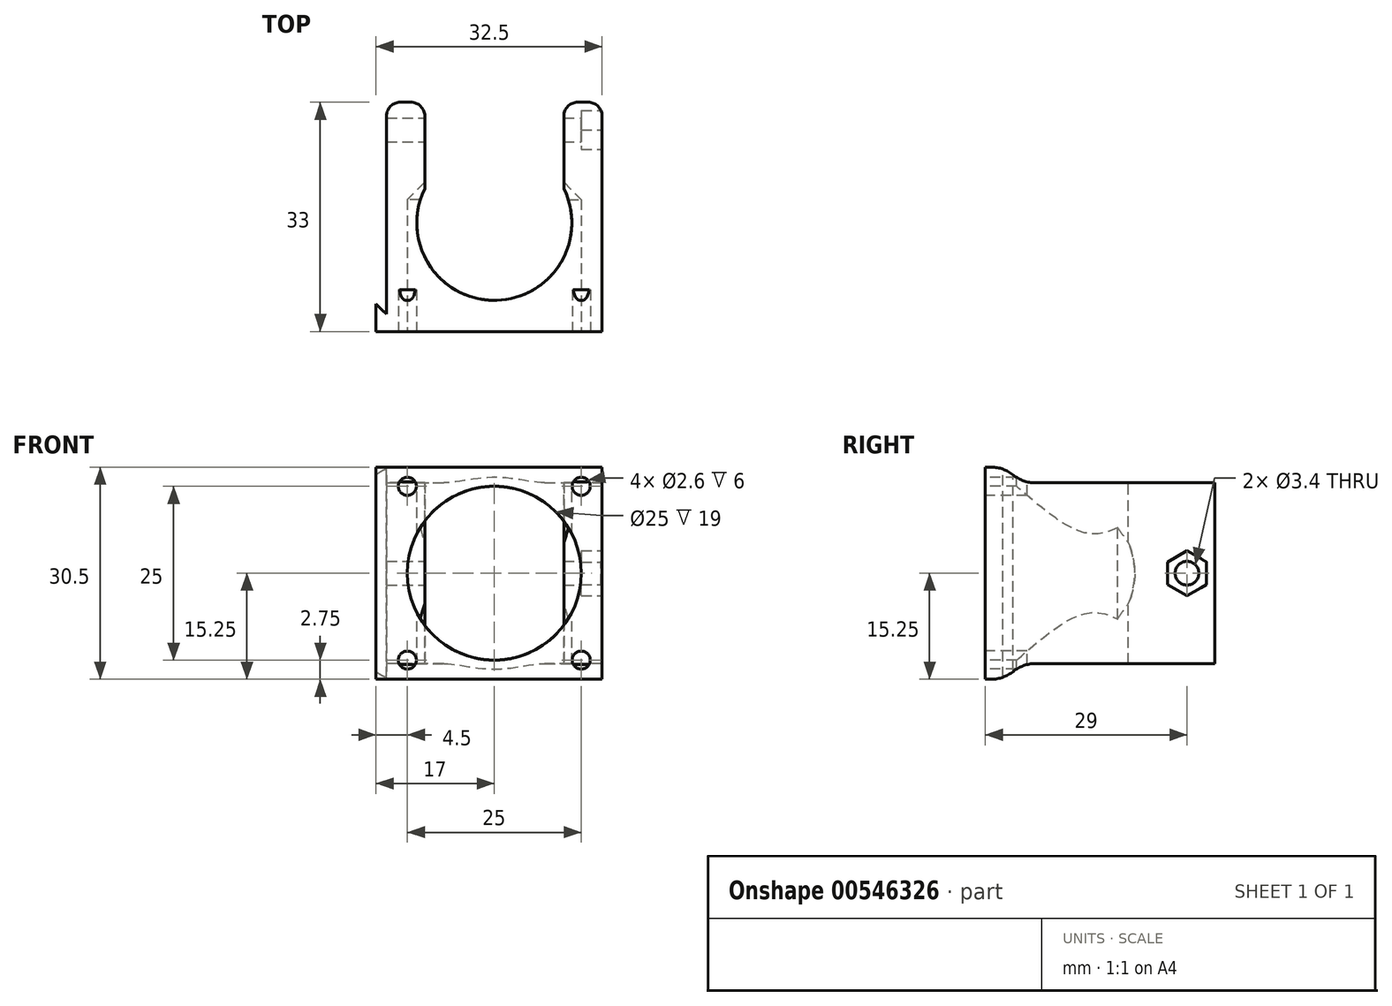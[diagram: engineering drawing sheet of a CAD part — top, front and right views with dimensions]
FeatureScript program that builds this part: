
annotation { "Feature Type Name" : "Feature", "Feature Type Description" : "" }
export const myFeature = defineFeature(function(context is Context, id is Id, definition is map)
    precondition{}
    {
        {
            var Q0;
            Q0=qCreatedBy(makeId("Top.planeOp"),FACE);
            var sketch = newSketch(context, id + "F0", { "sketchPlane" : qUnion([Q0])});
            skLineSegment(sketch, "E0.bottom", {"start": v(15.5, 16.5) * mm, "end": v(-15.5, 16.5) * mm});
            skLineSegment(sketch, "E0.top", {"start": v(15.5, -16.5) * mm, "end": v(-15.5, -16.5) * mm});
            skLineSegment(sketch, "E0.left", {"start": v(15.5, 16.5) * mm, "end": v(15.5, -16.5) * mm});
            skLineSegment(sketch, "E0.right", {"start": v(-15.5, 16.5) * mm, "end": v(-15.5, -16.5) * mm});
            skPoint(sketch, "E0.middle", {"position": v(0, 0) * mm});
            skLineSegment(sketch, "E1.bottom", {"start": v(-10, 16.5) * mm, "end": v(10, 16.5) * mm});
            skLineSegment(sketch, "E1.top", {"start": v(-10, 3.5) * mm, "end": v(10, 3.5) * mm});
            skLineSegment(sketch, "E1.left", {"start": v(-10, 16.5) * mm, "end": v(-10, 3.5) * mm});
            skLineSegment(sketch, "E1.right", {"start": v(10, 16.5) * mm, "end": v(10, 3.5) * mm});
            skSolve(sketch);
        }
        {
            var Q0;
            {var subQ0=sQuery(id+"F0.wireOp",EDGE,"E0.top");Q0=makeQuery(id+"F0.imprint","IMPRINT",FACE,{"disambiguationData":[TD([[makeQuery(id+"F0.imprint","IMPRINT",EDGE,{"derivedFrom":subQ0}),-1.0]])]});}
            extrude(context, id + "F1", {"entities" : qUnion([Q0]), "depth" : 30.5 * mm, "offsetDistance" : 25 * mm});
        }
        {
            var Q0;
            Q0=makeQuery(id+"F1.opExtrude","SWEPT_FACE",FACE,{"disambiguationData":[OSD([sQuery(id+"F0.wireOp",EDGE,"E0.top")])]});
            var sketch = newSketch(context, id + "F2", { "sketchPlane" : qUnion([Q0])});
            skCircle(sketch, "E2", {"center": v(0, 15.25) * mm, "radius": 12.5 * mm});
            skLineSegment(sketch, "E3", {"start": v(0, 15.25) * mm, "end": v(0, 30.5) * mm, "construction": true});
            skSolve(sketch);
        }
        {
            var Q0;
            Q0=makeQuery(id+"F2.imprint","IMPRINT",FACE,{"disambiguationData":[TD([[makeQuery(id+"F2.imprint","IMPRINT",EDGE,{"derivedFrom":sQuery(id+"F2.wireOp",EDGE,"E2")}),1.0]])]});
            extrude(context, id + "F3", {"entities" : qUnion([Q0]), "operationType" : NewBodyOperationType.REMOVE, "oppositeDirection" : true, "depth" : 22 * mm, "offsetDistance" : 25 * mm});
        }
        {
            var Q0;
            Q0=makeQuery(id+"F1.opExtrude","SWEPT_FACE",FACE,{"disambiguationData":[OSD([sQuery(id+"F0.wireOp",EDGE,"E0.right")])]});
            var sketch = newSketch(context, id + "F4", { "sketchPlane" : qUnion([Q0])});
            skSolve(sketch);
        }
        {
            var Q0;
            {var subQ0=sQuery(id+"F0.wireOp",EDGE,"E0.right");Q0=makeQuery(id+"F4.imprint","IMPRINT",FACE,{"disambiguationData":[TD([[makeQuery(id+"F4.imprint","IMPRINT",EDGE,{"derivedFrom":makeQuery(id+"F1.opExtrude","CAP_EDGE",EDGE,{"disambiguationData":[OSD([subQ0])],"isStart":true})}),1.0]])]});}
            var sketch = newSketch(context, id + "F5", { "sketchPlane" : qUnion([Q0])});
            skLineSegment(sketch, "E4.bottom", {"start": v(13.5, 0) * mm, "end": v(-21.5, 0) * mm});
            skLineSegment(sketch, "E4.top", {"start": v(13.5, 2.25) * mm, "end": v(-21.5, 2.25) * mm});
            skLineSegment(sketch, "E4.left", {"start": v(13.5, 0) * mm, "end": v(13.5, 2.25) * mm});
            skLineSegment(sketch, "E4.right", {"start": v(-21.5, 0) * mm, "end": v(-21.5, 2.25) * mm});
            skLineSegment(sketch, "E5.bottom", {"start": v(13.5, 28.25) * mm, "end": v(-21.5, 28.25) * mm});
            skLineSegment(sketch, "E5.top", {"start": v(13.5, 30.5) * mm, "end": v(-21.5, 30.5) * mm});
            skLineSegment(sketch, "E5.left", {"start": v(13.5, 28.25) * mm, "end": v(13.5, 30.5) * mm});
            skLineSegment(sketch, "E5.right", {"start": v(-21.5, 28.25) * mm, "end": v(-21.5, 30.5) * mm});
            skSolve(sketch);
        }
        {
            var Q0;
            {var subQ4=sQuery(id+"F5.wireOp",EDGE,"E4.right");Q0=makeQuery(id+"F5.imprint","IMPRINT",FACE,{"disambiguationData":[TD([[makeQuery(id+"F5.imprint","IMPRINT",EDGE,{"derivedFrom":subQ4}),-1.0]])]});}
            var Q1;
            {var subQ4=sQuery(id+"F5.wireOp",EDGE,"E4.left");Q1=makeQuery(id+"F5.imprint","IMPRINT",FACE,{"disambiguationData":[TD([[makeQuery(id+"F5.imprint","IMPRINT",EDGE,{"derivedFrom":subQ4}),1.0]])]});}
            var Q2;
            {var subQ0=sQuery(id+"F5.wireOp",EDGE,"E5.left");Q2=makeQuery(id+"F5.imprint","IMPRINT",FACE,{"disambiguationData":[TD([[makeQuery(id+"F5.imprint","IMPRINT",EDGE,{"derivedFrom":subQ0}),1.0]])]});}
            extrude(context, id + "F6", {"entities" : qUnion([Q0, Q1, Q2]), "operationType" : NewBodyOperationType.REMOVE, "oppositeDirection" : true, "depth" : 50 * mm, "offsetDistance" : 25 * mm});
        }
        {
            var Q0;
            {var subQ0=sQuery(id+"F5.wireOp",EDGE,"E4.top");var subQ1=sQuery(id+"F5.wireOp",EDGE,"E4.left");Q0=makeQuery(id+"F6.boolean.opBoolean","COPY",EDGE,{"disambiguationData":[TD([makeQuery(id+"F1.opExtrude","SWEPT_FACE",FACE,{"disambiguationData":[OSD([sQuery(id+"F0.wireOp",EDGE,"E0.right")])]})])],"derivedFrom":makeQuery(id+"F6.opExtrude","SWEPT_EDGE",EDGE,{"disambiguationData":[OSD([subQ0,subQ1])]})});}
            var Q1;
            {var subQ0=sQuery(id+"F5.wireOp",EDGE,"E4.top");var subQ1=sQuery(id+"F5.wireOp",EDGE,"E4.left");Q1=makeQuery(id+"F6.boolean.opBoolean","COPY",EDGE,{"disambiguationData":[TD([makeQuery(id+"F1.opExtrude","SWEPT_FACE",FACE,{"disambiguationData":[OSD([sQuery(id+"F0.wireOp",EDGE,"E0.left")])]})])],"derivedFrom":makeQuery(id+"F6.opExtrude","SWEPT_EDGE",EDGE,{"disambiguationData":[OSD([subQ0,subQ1])]})});}
            var Q2;
            Q2=makeQuery(id+"F6.boolean.opBoolean","COPY",EDGE,{"derivedFrom":makeQuery(id+"F6.opExtrude","SWEPT_EDGE",EDGE,{"disambiguationData":[OSD([sQuery(id+"F5.wireOp",EDGE,"E5.bottom"),sQuery(id+"F5.wireOp",EDGE,"E5.left")])]})});
            fillet(context, id + "F7", {"entities" : qUnion([Q0, Q1, Q2]), "radius" : 5 * mm, "tangentPropagation" : true, "allowEdgeOverflow" : false});
        }
        {
            var Q0;
            Q0=makeQuery(id+"F1.opExtrude","SWEPT_FACE",FACE,{"disambiguationData":[OSD([sQuery(id+"F0.wireOp",EDGE,"E0.top")])]});
            var sketch = newSketch(context, id + "F8", { "sketchPlane" : qUnion([Q0])});
            skLineSegment(sketch, "E6.bottom", {"start": v(12.5, 27.75) * mm, "end": v(-12.5, 27.75) * mm, "construction": true});
            skLineSegment(sketch, "E6.top", {"start": v(12.5, 2.75) * mm, "end": v(-12.5, 2.75) * mm, "construction": true});
            skLineSegment(sketch, "E6.left", {"start": v(12.5, 27.75) * mm, "end": v(12.5, 2.75) * mm, "construction": true});
            skLineSegment(sketch, "E6.right", {"start": v(-12.5, 27.75) * mm, "end": v(-12.5, 2.75) * mm, "construction": true});
            skPoint(sketch, "E6.middle", {"position": v(0, 15.25) * mm});
            skCircle(sketch, "E7", {"center": v(-12.5, 27.75) * mm, "radius": 1.3 * mm});
            skCircle(sketch, "E8", {"center": v(12.5, 27.75) * mm, "radius": 1.3 * mm});
            skCircle(sketch, "E9", {"center": v(12.5, 2.75) * mm, "radius": 1.3 * mm});
            skCircle(sketch, "E10", {"center": v(-12.5, 2.75) * mm, "radius": 1.3 * mm});
            skSolve(sketch);
        }
        {
            var Q0;
            Q0=makeQuery(id+"F1.opExtrude","CAP_FACE",FACE,{"disambiguationData":[OSD([sQuery(id+"F0.wireOp",EDGE,"E0.bottom"),sQuery(id+"F0.wireOp",EDGE,"E0.top"),sQuery(id+"F0.wireOp",EDGE,"E0.left"),sQuery(id+"F0.wireOp",EDGE,"E0.right"),sQuery(id+"F0.wireOp",EDGE,"E1.top"),sQuery(id+"F0.wireOp",EDGE,"E1.left"),sQuery(id+"F0.wireOp",EDGE,"E1.right")])],"isStart":false});
            var sketch = newSketch(context, id + "F9", { "sketchPlane" : qUnion([Q0])});
            skCircle(sketch, "E11", {"center": v(0, -0.85) * mm, "radius": 11.15 * mm});
            skSolve(sketch);
        }
        {
            var Q0;
            Q0=makeQuery(id+"F9.imprint","IMPRINT",FACE,{"disambiguationData":[TD([[makeQuery(id+"F9.imprint","IMPRINT",EDGE,{"derivedFrom":sQuery(id+"F9.wireOp",EDGE,"E11")}),1.0]])]});
            extrude(context, id + "F10", {"entities" : qUnion([Q0]), "operationType" : NewBodyOperationType.REMOVE, "oppositeDirection" : true, "depth" : 50 * mm, "offsetDistance" : 25 * mm});
        }
        {
            var Q0;
            Q0=qSketchRegion(id+"F8",true);
            extrude(context, id + "F11", {"entities" : qUnion([Q0]), "operationType" : NewBodyOperationType.REMOVE, "oppositeDirection" : true, "depth" : 6 * mm, "offsetDistance" : 25 * mm});
        }
        {
            var Q0;
            Q0=makeQuery(id+"F1.opExtrude","SWEPT_FACE",FACE,{"disambiguationData":[OSD([sQuery(id+"F0.wireOp",EDGE,"E0.left")])]});
            var sketch = newSketch(context, id + "F12", { "sketchPlane" : qUnion([Q0])});
            skCircle(sketch, "E12", {"center": v(12.5, 15.25) * mm, "radius": 1.7 * mm});
            skPoint(sketch, "E12.centerSnap0", {"position": v(16.5, 15.25) * mm});
            skCircle(sketch, "E13.cCircle", {"center": v(12.5, 15.25) * mm, "radius": 2.8 * mm, "construction": true});
            skLineSegment(sketch, "E13.0", {"start": v(12.5, 12.02) * mm, "end": v(9.7, 13.63) * mm});
            skLineSegment(sketch, "E13.1", {"start": v(9.7, 13.63) * mm, "end": v(9.7, 16.87) * mm});
            skLineSegment(sketch, "E13.2", {"start": v(9.7, 16.87) * mm, "end": v(12.5, 18.48) * mm});
            skLineSegment(sketch, "E13.3", {"start": v(12.5, 18.48) * mm, "end": v(15.3, 16.87) * mm});
            skLineSegment(sketch, "E13.4", {"start": v(15.3, 16.87) * mm, "end": v(15.3, 13.63) * mm});
            skLineSegment(sketch, "E13.5", {"start": v(15.3, 13.63) * mm, "end": v(12.5, 12.02) * mm});
            skPoint(sketch, "E13.0.midPoint", {"position": v(11.1, 12.83) * mm});
            skSolve(sketch);
        }
        {
            var Q0;
            Q0=makeQuery(id+"F12.imprint","IMPRINT",FACE,{"disambiguationData":[TD([[makeQuery(id+"F12.imprint","IMPRINT",EDGE,{"derivedFrom":sQuery(id+"F12.wireOp",EDGE,"E12")}),1.0]])]});
            extrude(context, id + "F13", {"entities" : qUnion([Q0]), "operationType" : NewBodyOperationType.REMOVE, "oppositeDirection" : true, "depth" : 50 * mm, "offsetDistance" : 25 * mm});
        }
        {
            var Q0;
            Q0=makeQuery(id+"F12.imprint","IMPRINT",FACE,{"disambiguationData":[TD([[makeQuery(id+"F12.imprint","IMPRINT",EDGE,{"derivedFrom":sQuery(id+"F12.wireOp",EDGE,"E12")}),-1.0]])]});
            extrude(context, id + "F14", {"entities" : qUnion([Q0]), "operationType" : NewBodyOperationType.REMOVE, "oppositeDirection" : true, "depth" : 3 * mm, "offsetDistance" : 25 * mm});
        }
        {
            var Q0;
            {var subQ0=sQuery(id+"F2.wireOp",EDGE,"E2");Q0=makeQuery(id+"F3.boolean.opBoolean","COPY",EDGE,{"disambiguationData":[TD([makeQuery(id+"F1.opExtrude","SWEPT_FACE",FACE,{"disambiguationData":[OSD([sQuery(id+"F0.wireOp",EDGE,"E1.left")])]})])],"derivedFrom":makeQuery(id+"F3.opExtrude","CAP_EDGE",EDGE,{"disambiguationData":[OSD([subQ0])],"isStart":false})});}
            var Q1;
            {var subQ0=sQuery(id+"F2.wireOp",EDGE,"E2");Q1=makeQuery(id+"F3.boolean.opBoolean","COPY",EDGE,{"disambiguationData":[TD([makeQuery(id+"F1.opExtrude","SWEPT_FACE",FACE,{"disambiguationData":[OSD([sQuery(id+"F0.wireOp",EDGE,"E1.right")])]})])],"derivedFrom":makeQuery(id+"F3.opExtrude","CAP_EDGE",EDGE,{"disambiguationData":[OSD([subQ0])],"isStart":false})});}
            chamfer(context, id + "F15", {"entities" : qUnion([Q0, Q1]), "width" : 3 * mm, "tangentPropagation" : true});
        }
        {
            var Q0;
            Q0=makeQuery(id+"F1.opExtrude","CAP_FACE",FACE,{"disambiguationData":[OSD([sQuery(id+"F0.wireOp",EDGE,"E0.bottom"),sQuery(id+"F0.wireOp",EDGE,"E0.top"),sQuery(id+"F0.wireOp",EDGE,"E0.left"),sQuery(id+"F0.wireOp",EDGE,"E0.right"),sQuery(id+"F0.wireOp",EDGE,"E1.top"),sQuery(id+"F0.wireOp",EDGE,"E1.left"),sQuery(id+"F0.wireOp",EDGE,"E1.right")])],"isStart":false});
            var sketch = newSketch(context, id + "F16", { "sketchPlane" : qUnion([Q0])});
            skLineSegment(sketch, "E14", {"start": v(-15.5, -16.5) * mm, "end": v(-17, -16.5) * mm});
            skLineSegment(sketch, "E15", {"start": v(-17, -16.5) * mm, "end": v(-17, -12.5) * mm});
            skLineSegment(sketch, "E16", {"start": v(-17, -12.5) * mm, "end": v(-15.5, -14) * mm});
            skSolve(sketch);
        }
        {
            var Q0;
            {var subQ0=sQuery(id+"F16.wireOp",EDGE,"E14");Q0=makeQuery(id+"F16.imprint","IMPRINT",FACE,{"disambiguationData":[TD([[makeQuery(id+"F16.imprint","IMPRINT",EDGE,{"derivedFrom":subQ0}),-1.0]])]});}
            var Q1;
            Q1=makeQuery(id+"F1.opExtrude","CAP_FACE",FACE,{"disambiguationData":[OSD([sQuery(id+"F0.wireOp",EDGE,"E0.bottom"),sQuery(id+"F0.wireOp",EDGE,"E0.top"),sQuery(id+"F0.wireOp",EDGE,"E0.left"),sQuery(id+"F0.wireOp",EDGE,"E0.right"),sQuery(id+"F0.wireOp",EDGE,"E1.top"),sQuery(id+"F0.wireOp",EDGE,"E1.left"),sQuery(id+"F0.wireOp",EDGE,"E1.right")])],"isStart":true});
            extrude(context, id + "F17", {"entities" : qUnion([Q0]), "operationType" : NewBodyOperationType.ADD, "endBound" : BoundingType.UP_TO_SURFACE, "oppositeDirection" : true, "depth" : 25 * mm, "endBoundEntityFace" : qUnion([Q1]), "offsetDistance" : 25 * mm});
        }
        {
            var Q0;
            Q0=makeQuery(id+"F1.opExtrude","SWEPT_EDGE",EDGE,{"disambiguationData":[OSD([sQuery(id+"F0.wireOp",EDGE,"E0.bottom"),sQuery(id+"F0.wireOp",EDGE,"E1.bottom"),sQuery(id+"F0.wireOp",EDGE,"E1.left")])]});
            var Q1;
            Q1=makeQuery(id+"F1.opExtrude","SWEPT_EDGE",EDGE,{"disambiguationData":[OSD([sQuery(id+"F0.wireOp",EDGE,"E0.bottom"),sQuery(id+"F0.wireOp",EDGE,"E0.right")])]});
            var Q2;
            Q2=makeQuery(id+"F1.opExtrude","SWEPT_EDGE",EDGE,{"disambiguationData":[OSD([sQuery(id+"F0.wireOp",EDGE,"E0.bottom"),sQuery(id+"F0.wireOp",EDGE,"E1.bottom"),sQuery(id+"F0.wireOp",EDGE,"E1.right")])]});
            var Q3;
            Q3=makeQuery(id+"F1.opExtrude","SWEPT_EDGE",EDGE,{"disambiguationData":[OSD([sQuery(id+"F0.wireOp",EDGE,"E0.bottom"),sQuery(id+"F0.wireOp",EDGE,"E0.left")])]});
            fillet(context, id + "F18", {"entities" : qUnion([Q0, Q1, Q2, Q3]), "radius" : 2 * mm, "tangentPropagation" : true, "allowEdgeOverflow" : false});
        }
        {
            var Q0;
            {var subQ0=sQuery(id+"F0.wireOp",EDGE,"E0.right");var subQ1=sQuery(id+"F0.wireOp",EDGE,"E0.left");var subQ2=makeQuery(id+"F1.opExtrude","CAP_FACE",FACE,{"disambiguationData":[OSD([sQuery(id+"F0.wireOp",EDGE,"E0.bottom"),sQuery(id+"F0.wireOp",EDGE,"E0.top"),subQ1,subQ0,sQuery(id+"F0.wireOp",EDGE,"E1.top"),sQuery(id+"F0.wireOp",EDGE,"E1.left"),sQuery(id+"F0.wireOp",EDGE,"E1.right")])],"isStart":true});var subQ3=sQuery(id+"F5.wireOp",EDGE,"E4.left");var subQ4=sQuery(id+"F5.wireOp",EDGE,"E4.top");Q0=makeQuery(id+"F10.boolean.opBoolean","SPLIT",EDGE,{"disambiguationData":[TD([makeQuery(id+"F1.opExtrude","SWEPT_FACE",FACE,{"disambiguationData":[OSD([subQ0])]})])],"derivedFrom":makeQuery(id+"F7.opFillet","BLEND_EDGE",EDGE,{"blendedFrom":[makeQuery(id+"F6.boolean.opBoolean","COPY",EDGE,{"disambiguationData":[TD([makeQuery(id+"F1.opExtrude","SWEPT_FACE",FACE,{"disambiguationData":[OSD([subQ1])]})])],"derivedFrom":makeQuery(id+"F6.opExtrude","SWEPT_EDGE",EDGE,{"disambiguationData":[OSD([subQ4,subQ3])]})}),subQ2],"blendedInto":[subQ2]})});}
            var Q1;
            Q1=makeQuery(id+"F7.opFillet","BLEND_EDGE",EDGE,{"blendedFrom":[makeQuery(id+"F6.boolean.opBoolean","COPY",EDGE,{"derivedFrom":makeQuery(id+"F6.opExtrude","SWEPT_EDGE",EDGE,{"disambiguationData":[OSD([sQuery(id+"F5.wireOp",EDGE,"E5.bottom"),sQuery(id+"F5.wireOp",EDGE,"E5.left")])]})}),makeQuery(id+"F1.opExtrude","CAP_FACE",FACE,{"disambiguationData":[OSD([sQuery(id+"F0.wireOp",EDGE,"E0.bottom"),sQuery(id+"F0.wireOp",EDGE,"E0.top"),sQuery(id+"F0.wireOp",EDGE,"E0.left"),sQuery(id+"F0.wireOp",EDGE,"E0.right"),sQuery(id+"F0.wireOp",EDGE,"E1.top"),sQuery(id+"F0.wireOp",EDGE,"E1.left"),sQuery(id+"F0.wireOp",EDGE,"E1.right")])],"isStart":false})],"blendedInto":[makeQuery(id+"F1.opExtrude","CAP_FACE",FACE,{"disambiguationData":[OSD([sQuery(id+"F0.wireOp",EDGE,"E0.bottom"),sQuery(id+"F0.wireOp",EDGE,"E0.top"),sQuery(id+"F0.wireOp",EDGE,"E0.left"),sQuery(id+"F0.wireOp",EDGE,"E0.right"),sQuery(id+"F0.wireOp",EDGE,"E1.top"),sQuery(id+"F0.wireOp",EDGE,"E1.left"),sQuery(id+"F0.wireOp",EDGE,"E1.right")])],"isStart":false})]});
            fillet(context, id + "F19", {"entities" : qUnion([Q0, Q1]), "radius" : 5 * mm, "tangentPropagation" : true, "allowEdgeOverflow" : false});
        }
    });
